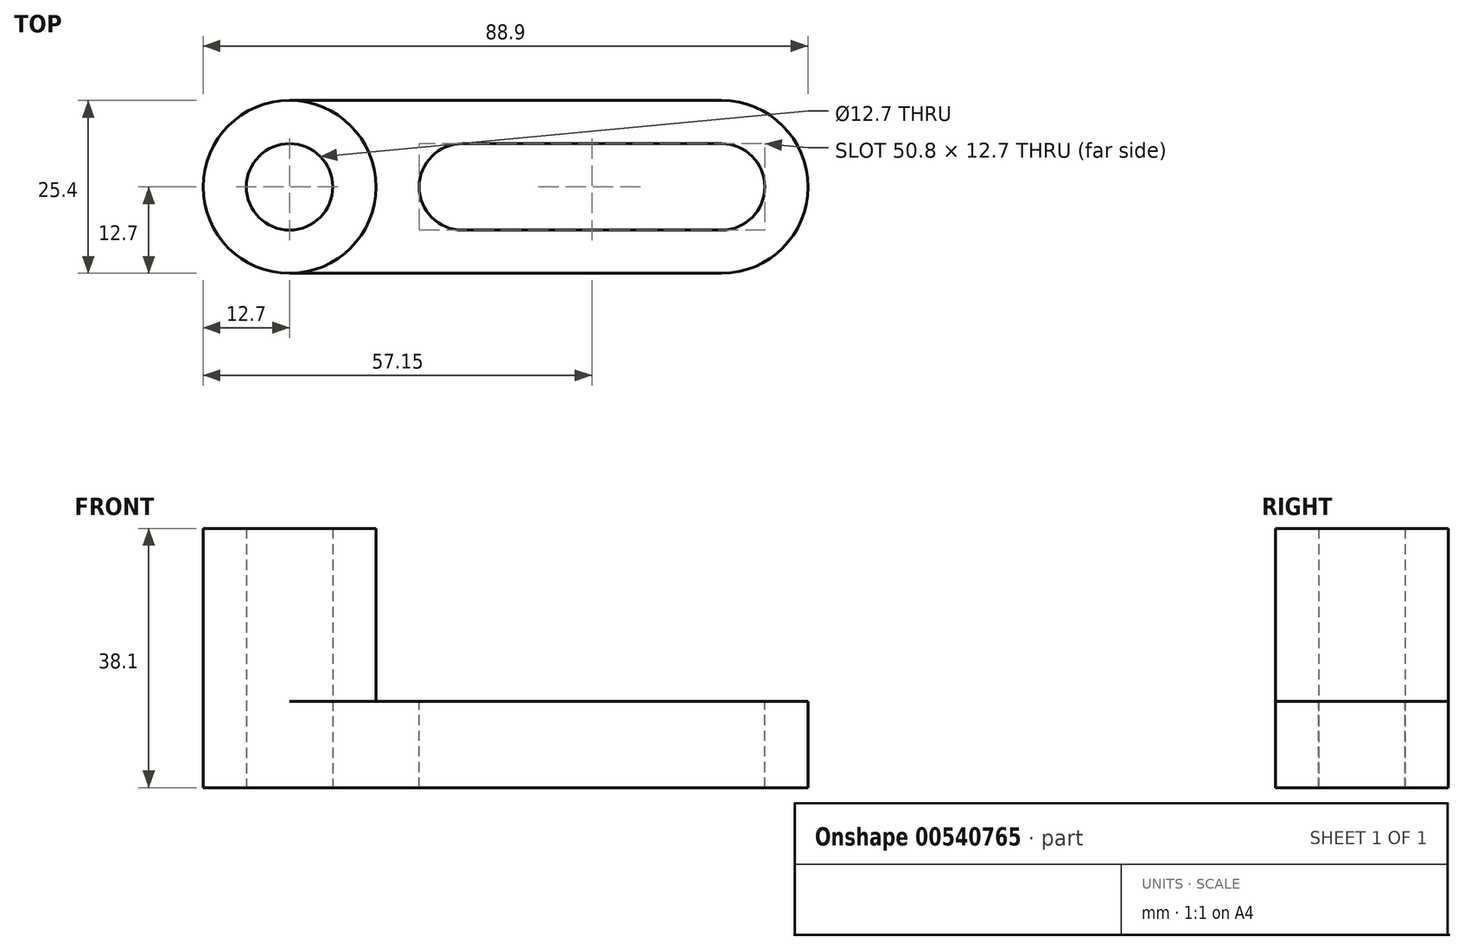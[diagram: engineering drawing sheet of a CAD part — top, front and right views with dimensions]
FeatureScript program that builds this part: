
annotation { "Feature Type Name" : "Feature", "Feature Type Description" : "" }
export const myFeature = defineFeature(function(context is Context, id is Id, definition is map)
    precondition{}
    {
        {
            var Q0;
            Q0=qCreatedBy(makeId("Front.planeOp"),FACE);
            var sketch = newSketch(context, id + "F0", { "sketchPlane" : qUnion([Q0])});
            skLineSegment(sketch, "E0", {"start": v(0, 0) * mm, "end": v(88.9, 0) * mm});
            skLineSegment(sketch, "E1", {"start": v(88.9, 0) * mm, "end": v(88.9, 12.7) * mm});
            skLineSegment(sketch, "E2", {"start": v(88.9, 12.7) * mm, "end": v(0, 12.7) * mm});
            skLineSegment(sketch, "E3", {"start": v(0, 12.7) * mm, "end": v(0, 0) * mm});
            skSolve(sketch);
        }
        {
            var Q0;
            Q0=makeQuery(id+"F0.imprint","IMPRINT",FACE,{"disambiguationData":[TD([[makeQuery(id+"F0.imprint","IMPRINT",EDGE,{"derivedFrom":sQuery(id+"F0.wireOp",EDGE,"E0")}),1.0]])]});
            extrude(context, id + "F1", {"entities" : qUnion([Q0]), "oppositeDirection" : true, "depth" : 25.4 * mm, "offsetDistance" : 25.4 * mm});
        }
        {
            var Q0;
            Q0=makeQuery(id+"F1.opExtrude","SWEPT_FACE",FACE,{"disambiguationData":[OSD([sQuery(id+"F0.wireOp",EDGE,"E2")])]});
            var sketch = newSketch(context, id + "F2", { "sketchPlane" : qUnion([Q0])});
            skCircle(sketch, "E4", {"center": v(12.7, 12.7) * mm, "radius": 12.7 * mm});
            skCircle(sketch, "E5", {"center": v(12.7, 12.7) * mm, "radius": 6.35 * mm});
            skSolve(sketch);
        }
        {
            var Q0;
            Q0=makeQuery(id+"F2.imprint","IMPRINT",FACE,{"disambiguationData":[TD([[makeQuery(id+"F2.imprint","IMPRINT",EDGE,{"derivedFrom":sQuery(id+"F2.wireOp",EDGE,"E5")}),-1.0]])]});
            extrude(context, id + "F3", {"entities" : qUnion([Q0]), "operationType" : NewBodyOperationType.ADD, "depth" : 25.4 * mm, "offsetDistance" : 25.4 * mm});
        }
        {
            var Q0;
            {var subQ0=sQuery(id+"F0.wireOp",EDGE,"E3");var subQ1=sQuery(id+"F0.wireOp",EDGE,"E2");var subQ2=makeQuery(id+"F1.opExtrude","SWEPT_FACE",FACE,{"disambiguationData":[OSD([subQ1])]});Q0=makeQuery(id+"F3.boolean.opBoolean","SPLIT",FACE,{"disambiguationData":[TD([makeQuery(id+"F1.opExtrude","CAP_FACE",FACE,{"disambiguationData":[OSD([sQuery(id+"F0.wireOp",EDGE,"E0"),sQuery(id+"F0.wireOp",EDGE,"E1"),subQ1,subQ0])],"isStart":false}),subQ2,makeQuery(id+"F1.opExtrude","SWEPT_FACE",FACE,{"disambiguationData":[OSD([subQ0])]}),makeQuery(id+"F3.opExtrude","SWEPT_FACE",FACE,{"disambiguationData":[OSD([sQuery(id+"F2.wireOp",EDGE,"E4")])]})])],"derivedFrom":subQ2});}
            var Q1;
            {var subQ0=sQuery(id+"F0.wireOp",EDGE,"E3");var subQ1=sQuery(id+"F0.wireOp",EDGE,"E2");var subQ2=makeQuery(id+"F1.opExtrude","SWEPT_FACE",FACE,{"disambiguationData":[OSD([subQ1])]});Q1=makeQuery(id+"F3.boolean.opBoolean","SPLIT",FACE,{"disambiguationData":[TD([makeQuery(id+"F1.opExtrude","CAP_FACE",FACE,{"disambiguationData":[OSD([sQuery(id+"F0.wireOp",EDGE,"E0"),sQuery(id+"F0.wireOp",EDGE,"E1"),subQ1,subQ0])],"isStart":true}),subQ2,makeQuery(id+"F1.opExtrude","SWEPT_FACE",FACE,{"disambiguationData":[OSD([subQ0])]}),makeQuery(id+"F3.opExtrude","SWEPT_FACE",FACE,{"disambiguationData":[OSD([sQuery(id+"F2.wireOp",EDGE,"E4")])]})])],"derivedFrom":subQ2});}
            extrude(context, id + "F4", {"entities" : qUnion([Q0, Q1]), "operationType" : NewBodyOperationType.REMOVE, "oppositeDirection" : true, "depth" : 62.23 * mm, "offsetDistance" : 25.4 * mm});
        }
        {
            var Q0;
            {var subQ0=sQuery(id+"F0.wireOp",EDGE,"E2");var subQ1=makeQuery(id+"F1.opExtrude","SWEPT_FACE",FACE,{"disambiguationData":[OSD([subQ0])]});var subQ2=sQuery(id+"F0.wireOp",EDGE,"E1");var subQ3=sQuery(id+"F0.wireOp",EDGE,"E3");var subQ4=sQuery(id+"F0.wireOp",EDGE,"E0");Q0=makeQuery(id+"F3.boolean.opBoolean","SPLIT",FACE,{"disambiguationData":[TD([makeQuery(id+"F1.opExtrude","CAP_FACE",FACE,{"disambiguationData":[OSD([subQ4,subQ2,subQ0,subQ3])],"isStart":true}),makeQuery(id+"F1.opExtrude","CAP_FACE",FACE,{"disambiguationData":[OSD([subQ4,subQ2,subQ0,subQ3])],"isStart":false}),makeQuery(id+"F1.opExtrude","SWEPT_FACE",FACE,{"disambiguationData":[OSD([subQ2])]}),subQ1,makeQuery(id+"F3.opExtrude","SWEPT_FACE",FACE,{"disambiguationData":[OSD([sQuery(id+"F2.wireOp",EDGE,"E4")])]})])],"derivedFrom":subQ1});}
            var sketch = newSketch(context, id + "F5", { "sketchPlane" : qUnion([Q0])});
            skLineSegment(sketch, "E6", {"start": v(38.1, 19.05) * mm, "end": v(76.2, 19.05) * mm});
            skLineSegment(sketch, "E7", {"start": v(38.1, 6.35) * mm, "end": v(76.2, 6.35) * mm});
            skArc(sketch, "E8", {"start": v(38.1, 19.05) * mm, "mid": v(31.75, 12.7) * mm, "end": v(38.1, 6.35) * mm});
            skArc(sketch, "E9", {"start": v(76.2, 6.35) * mm, "mid": v(82.55, 12.7) * mm, "end": v(76.2, 19.05) * mm});
            skSolve(sketch);
        }
        {
            var Q0;
            Q0=makeQuery(id+"F5.imprint","IMPRINT",FACE,{"disambiguationData":[TD([[makeQuery(id+"F5.imprint","IMPRINT",EDGE,{"derivedFrom":sQuery(id+"F5.wireOp",EDGE,"E6")}),-1.0]])]});
            extrude(context, id + "F6", {"entities" : qUnion([Q0]), "operationType" : NewBodyOperationType.REMOVE, "oppositeDirection" : true, "depth" : 25.4 * mm, "offsetDistance" : 25.4 * mm});
        }
        {
            var Q0;
            {var subQ0=sQuery(id+"F0.wireOp",EDGE,"E2");var subQ1=makeQuery(id+"F1.opExtrude","SWEPT_FACE",FACE,{"disambiguationData":[OSD([subQ0])]});var subQ2=sQuery(id+"F0.wireOp",EDGE,"E1");var subQ3=sQuery(id+"F0.wireOp",EDGE,"E3");var subQ4=sQuery(id+"F0.wireOp",EDGE,"E0");Q0=makeQuery(id+"F3.boolean.opBoolean","SPLIT",FACE,{"disambiguationData":[TD([makeQuery(id+"F1.opExtrude","CAP_FACE",FACE,{"disambiguationData":[OSD([subQ4,subQ2,subQ0,subQ3])],"isStart":true}),makeQuery(id+"F1.opExtrude","CAP_FACE",FACE,{"disambiguationData":[OSD([subQ4,subQ2,subQ0,subQ3])],"isStart":false}),makeQuery(id+"F1.opExtrude","SWEPT_FACE",FACE,{"disambiguationData":[OSD([subQ2])]}),subQ1,makeQuery(id+"F3.opExtrude","SWEPT_FACE",FACE,{"disambiguationData":[OSD([sQuery(id+"F2.wireOp",EDGE,"E4")])]})])],"derivedFrom":subQ1});}
            var sketch = newSketch(context, id + "F7", { "sketchPlane" : qUnion([Q0])});
            skArc(sketch, "E10", {"start": v(76.2, 0) * mm, "mid": v(88.9, 12.7) * mm, "end": v(76.2, 25.4) * mm});
            skSolve(sketch);
        }
        {
            var Q0;
            {var subQ0=sQuery(id+"F7.wireOp",EDGE,"E10");var subQ1=sQuery(id+"F0.wireOp",EDGE,"E2");var subQ2=sQuery(id+"F0.wireOp",EDGE,"E1");var subQ5=makeQuery(id+"F1.opExtrude","SWEPT_EDGE",EDGE,{"disambiguationData":[OSD([subQ2,subQ1])]});var subQ6=makeQuery(id+"F7.imprint","INTERSECT",VERTEX,{"derivedFrom":[subQ5,subQ0]});Q0=makeQuery(id+"F7.imprint","IMPRINT",FACE,{"disambiguationData":[TD([[makeQuery(id+"F7.imprint","IMPRINT",EDGE,{"disambiguationData":[TD([[subQ6,-1.0]])],"derivedFrom":subQ0}),-1.0]])]});}
            var Q1;
            {var subQ0=sQuery(id+"F7.wireOp",EDGE,"E10");var subQ1=sQuery(id+"F0.wireOp",EDGE,"E2");var subQ2=sQuery(id+"F0.wireOp",EDGE,"E1");var subQ5=makeQuery(id+"F1.opExtrude","SWEPT_EDGE",EDGE,{"disambiguationData":[OSD([subQ2,subQ1])]});var subQ6=makeQuery(id+"F7.imprint","INTERSECT",VERTEX,{"derivedFrom":[subQ5,subQ0]});Q1=makeQuery(id+"F7.imprint","IMPRINT",FACE,{"disambiguationData":[TD([[makeQuery(id+"F7.imprint","IMPRINT",EDGE,{"disambiguationData":[TD([[subQ6,1.0]])],"derivedFrom":subQ0}),-1.0]])]});}
            extrude(context, id + "F8", {"entities" : qUnion([Q0, Q1]), "operationType" : NewBodyOperationType.REMOVE, "oppositeDirection" : true, "depth" : 25.4 * mm, "offsetDistance" : 25.4 * mm});
        }
        {
            var Q0;
            Q0=makeQuery(id+"F3.boolean.opBoolean","SPLIT",FACE,{"disambiguationData":[TD([makeQuery(id+"F3.opExtrude","SWEPT_FACE",FACE,{"disambiguationData":[OSD([sQuery(id+"F2.wireOp",EDGE,"E5")])]})])],"derivedFrom":makeQuery(id+"F1.opExtrude","SWEPT_FACE",FACE,{"disambiguationData":[OSD([sQuery(id+"F0.wireOp",EDGE,"E2")])]})});
            extrude(context, id + "F9", {"entities" : qUnion([Q0]), "operationType" : NewBodyOperationType.REMOVE, "oppositeDirection" : true, "depth" : 25.4 * mm, "offsetDistance" : 25.4 * mm});
        }
    });
